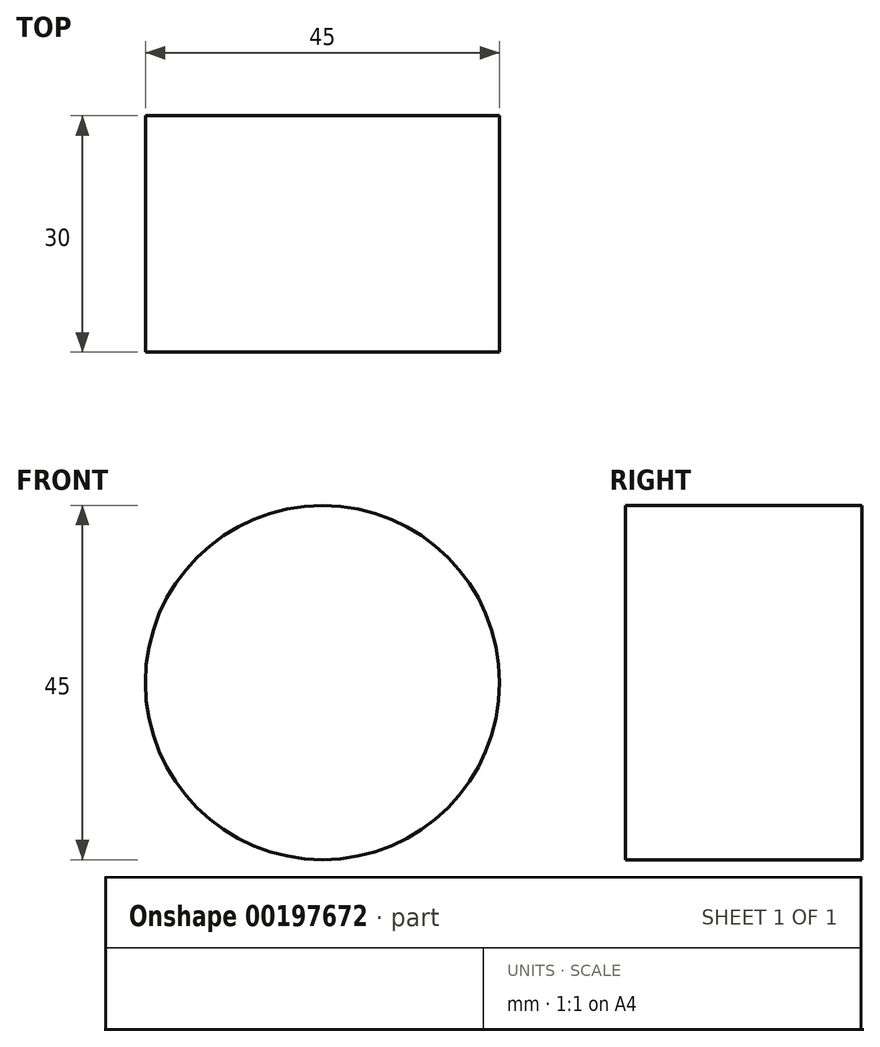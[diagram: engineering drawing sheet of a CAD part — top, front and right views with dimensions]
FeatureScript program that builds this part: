
annotation { "Feature Type Name" : "Feature", "Feature Type Description" : "" }
export const myFeature = defineFeature(function(context is Context, id is Id, definition is map)
    precondition{}
    {
        {
            var Q0;
            Q0=qCreatedBy(makeId("Front.planeOp"),FACE);
            var sketch = newSketch(context, id + "F0", { "sketchPlane" : qUnion([Q0])});
            skCircle(sketch, "E0", {"center": v(0, 0) * mm, "radius": 22.5 * mm});
            skSolve(sketch);
        }
        {
            var Q0;
            Q0 = qSketchRegion(id + "F0", true);
            extrude(context, id + "F1", {"entities" : qUnion([Q0]), "depth" : 30 * mm});
        }
    });
